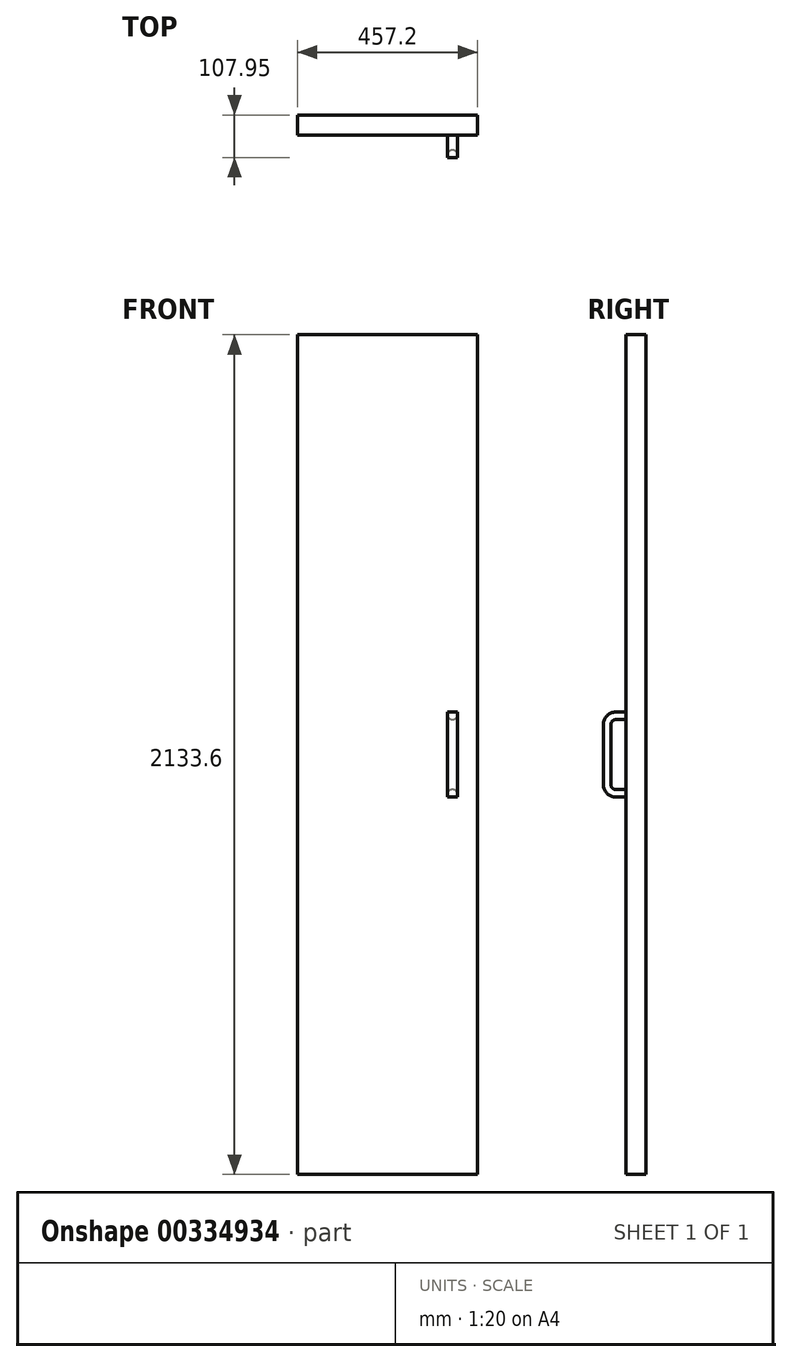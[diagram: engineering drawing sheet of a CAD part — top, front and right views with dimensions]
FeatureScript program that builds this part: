
annotation { "Feature Type Name" : "Feature", "Feature Type Description" : "" }
export const myFeature = defineFeature(function(context is Context, id is Id, definition is map)
    precondition{}
    {
        {
            var Q0;
            Q0=qCreatedBy(makeId("Front.planeOp"),FACE);
            var sketch = newSketch(context, id + "F0", { "sketchPlane" : qUnion([Q0])});
            skLineSegment(sketch, "E0.bottom", {"start": v(228.6, -1066.8) * mm, "end": v(-228.6, -1066.8) * mm});
            skLineSegment(sketch, "E0.top", {"start": v(228.6, 1066.8) * mm, "end": v(-228.6, 1066.8) * mm});
            skLineSegment(sketch, "E0.left", {"start": v(228.6, -1066.8) * mm, "end": v(228.6, 1066.8) * mm});
            skLineSegment(sketch, "E0.right", {"start": v(-228.6, -1066.8) * mm, "end": v(-228.6, 1066.8) * mm});
            skPoint(sketch, "E0.middle", {"position": v(0, 0) * mm});
            skSolve(sketch);
        }
        {
            var Q0;
            Q0=makeQuery(id+"F0.imprint","IMPRINT",FACE,{"disambiguationData":[TD([[makeQuery(id+"F0.imprint","IMPRINT",EDGE,{"derivedFrom":sQuery(id+"F0.wireOp",EDGE,"E0.bottom")}),-1.0]])]});
            extrude(context, id + "F1", {"entities" : qUnion([Q0]), "depth" : 50.8 * mm});
        }
        {
            var Q0;
            Q0=makeQuery(id+"F1.opExtrude","SWEPT_FACE",FACE,{"disambiguationData":[OSD([sQuery(id+"F0.wireOp",EDGE,"E0.left")])]});
            cPlane(context, id + "F2", {"entities" : qUnion([Q0]), "cplaneType" : CPlaneType.OFFSET, "offset" : 63.5 * mm, "oppositeDirection" : true, "width" : 150 * mm, "height" : 150 * mm});
        }
        {
            var Q0;
            Q0=qCreatedBy(id+"F2.planeOp",FACE);
            var sketch = newSketch(context, id + "F3", { "sketchPlane" : qUnion([Q0])});
            skLineSegment(sketch, "E1", {"start": v(-50.8, -101.6) * mm, "end": v(-76.6, -101.6) * mm});
            skArc(sketch, "E2", {"start": v(-101.6, -76.6) * mm, "mid": v(-94.28, -94.28) * mm, "end": v(-76.6, -101.6) * mm});
            skLineSegment(sketch, "E3", {"start": v(-101.6, -76.6) * mm, "end": v(-101.6, 76.6) * mm});
            skArc(sketch, "E4", {"start": v(-76.6, 101.6) * mm, "mid": v(-94.28, 94.28) * mm, "end": v(-101.6, 76.6) * mm});
            skLineSegment(sketch, "E5", {"start": v(-76.6, 101.6) * mm, "end": v(-50.8, 101.6) * mm});
            skLineSegment(sketch, "E6", {"start": v(-227.1, 0) * mm, "end": v(154.71, 0) * mm, "construction": true});
            skSolve(sketch);
        }
        {
            var Q0;
            Q0=makeQuery(id+"F1.opExtrude","CAP_FACE",FACE,{"disambiguationData":[OSD([sQuery(id+"F0.wireOp",EDGE,"E0.bottom"),sQuery(id+"F0.wireOp",EDGE,"E0.top"),sQuery(id+"F0.wireOp",EDGE,"E0.left"),sQuery(id+"F0.wireOp",EDGE,"E0.right")])],"isStart":false});
            var sketch = newSketch(context, id + "F4", { "sketchPlane" : qUnion([Q0])});
            skLineSegment(sketch, "E7", {"start": v(152.4, 107.95) * mm, "end": v(177.8, 107.95) * mm});
            skLineSegment(sketch, "E8", {"start": v(177.8, 107.95) * mm, "end": v(177.8, 101.6) * mm});
            skLineSegment(sketch, "E9", {"start": v(152.4, 107.95) * mm, "end": v(152.4, 101.6) * mm});
            skArc(sketch, "E10", {"start": v(152.4, 101.6) * mm, "mid": v(165.1, 88.9) * mm, "end": v(177.8, 101.6) * mm});
            skSolve(sketch);
        }
        {
            var Q0;
            Q0=makeQuery(id+"F4.imprint","IMPRINT",FACE,{"disambiguationData":[TD([[makeQuery(id+"F4.imprint","IMPRINT",EDGE,{"derivedFrom":sQuery(id+"F4.wireOp",EDGE,"E7")}),-1.0]])]});
            var Q1;
            Q1=sQuery(id+"F3.wireOp",EDGE,"E5");
            var Q2;
            Q2=sQuery(id+"F3.wireOp",EDGE,"E4");
            var Q3;
            Q3=sQuery(id+"F3.wireOp",EDGE,"E3");
            var Q4;
            Q4=sQuery(id+"F3.wireOp",EDGE,"E2");
            var Q5;
            Q5=sQuery(id+"F3.wireOp",EDGE,"E1");
            sweep(context, id + "F5", {"operationType" : NewBodyOperationType.ADD, "profiles" : qUnion([Q0]), "path" : qUnion([Q1, Q2, Q3, Q4, Q5])});
        }
    });
